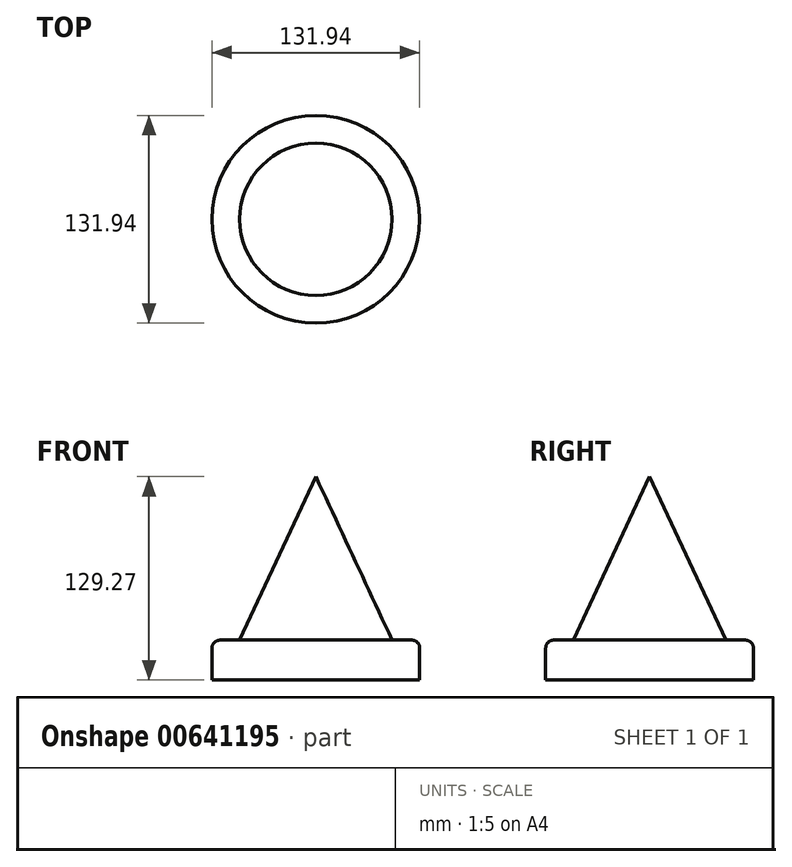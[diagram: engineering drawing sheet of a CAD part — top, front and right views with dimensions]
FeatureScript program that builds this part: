
annotation { "Feature Type Name" : "Feature", "Feature Type Description" : "" }
export const myFeature = defineFeature(function(context is Context, id is Id, definition is map)
    precondition{}
    {
        {
            var Q0;
            Q0=qCreatedBy(makeId("Top.planeOp"),FACE);
            var sketch = newSketch(context, id + "F0", { "sketchPlane" : qUnion([Q0])});
            skCircle(sketch, "E0", {"center": v(0, 0) * mm, "radius": 65.97 * mm});
            skSolve(sketch);
        }
        {
            var Q0;
            Q0=makeQuery(id+"F0.imprint","IMPRINT",FACE,{"disambiguationData":[TD([[makeQuery(id+"F0.imprint","IMPRINT",EDGE,{"derivedFrom":sQuery(id+"F0.wireOp",EDGE,"E0")}),1.0]])]});
            extrude(context, id + "F1", {"entities" : qUnion([Q0]), "depth" : 25.4 * mm, "offsetDistance" : 25.4 * mm});
        }
        {
            var Q0;
            Q0=qCreatedBy(makeId("Top.planeOp"),FACE);
            var sketch = newSketch(context, id + "F2", { "sketchPlane" : qUnion([Q0])});
            skCircle(sketch, "E1", {"center": v(0, 0) * mm, "radius": 57.16 * mm});
            skSolve(sketch);
        }
        {
            var Q0;
            Q0 = qSketchRegion(id + "F2", true);
            extrude(context, id + "F3", {"entities" : qUnion([Q0]), "operationType" : NewBodyOperationType.REMOVE, "oppositeDirection" : true, "depth" : 17.78 * mm, "offsetDistance" : 25.4 * mm});
        }
        {
            var Q0;
            Q0=makeQuery(id+"F1.opExtrude","CAP_FACE",FACE,{"disambiguationData":[OSD([sQuery(id+"F0.wireOp",EDGE,"E0")])],"isStart":false});
            var sketch = newSketch(context, id + "F4", { "sketchPlane" : qUnion([Q0])});
            skCircle(sketch, "E2", {"center": v(0, 0) * mm, "radius": 55.56 * mm});
            skSolve(sketch);
        }
        {
            var Q0;
            Q0=makeQuery(id+"F4.imprint","IMPRINT",FACE,{"disambiguationData":[TD([[makeQuery(id+"F4.imprint","IMPRINT",EDGE,{"derivedFrom":sQuery(id+"F4.wireOp",EDGE,"E2")}),1.0]])]});
            var sketch = newSketch(context, id + "F5", { "sketchPlane" : qUnion([Q0])});
            skSolve(sketch);
        }
        {
            var Q0;
            Q0=makeQuery(id+"F4.imprint","IMPRINT",FACE,{"disambiguationData":[TD([[makeQuery(id+"F4.imprint","IMPRINT",EDGE,{"derivedFrom":sQuery(id+"F4.wireOp",EDGE,"E2")}),1.0]])]});
            var Q1;
            Q1=makeQuery(id+"F4.imprint","IMPRINT",FACE,{"disambiguationData":[TD([[makeQuery(id+"F4.imprint","IMPRINT",EDGE,{"derivedFrom":sQuery(id+"F4.wireOp",EDGE,"E2")}),-1.0]])]});
            extrude(context, id + "F6", {"entities" : qUnion([Q0, Q1]), "operationType" : NewBodyOperationType.REMOVE, "depth" : 65.85 * mm, "offsetDistance" : 25.4 * mm});
        }
        {
            var Q0;
            Q0=makeQuery(id+"F1.opExtrude","CAP_EDGE",EDGE,{"disambiguationData":[OSD([sQuery(id+"F0.wireOp",EDGE,"E0")])],"isStart":false});
            fillet(context, id + "F7", {"entities" : qUnion([Q0]), "radius" : 5.08 * mm, "tangentPropagation" : true, "allowEdgeOverflow" : false});
        }
        {
            var Q0;
            Q0=qCreatedBy(makeId("Top.planeOp"),FACE);
            var sketch = newSketch(context, id + "F8", { "sketchPlane" : qUnion([Q0])});
            skCircle(sketch, "E3", {"center": v(0, 0) * mm, "radius": 62.08 * mm});
            skSolve(sketch);
        }
        {
            var Q0;
            Q0=makeQuery(id+"F8.imprint","IMPRINT",FACE,{"disambiguationData":[TD([[makeQuery(id+"F8.imprint","IMPRINT",EDGE,{"derivedFrom":sQuery(id+"F8.wireOp",EDGE,"E3")}),1.0]])]});
            var sketch = newSketch(context, id + "F9", { "sketchPlane" : qUnion([Q0])});
            skCircle(sketch, "E4", {"center": v(0, 0) * mm, "radius": 61.03 * mm});
            skSolve(sketch);
        }
        {
            var Q0;
            Q0=makeQuery(id+"F9.imprint","IMPRINT",FACE,{"disambiguationData":[TD([[makeQuery(id+"F9.imprint","IMPRINT",EDGE,{"derivedFrom":sQuery(id+"F9.wireOp",EDGE,"E4")}),1.0]])]});
            var sketch = newSketch(context, id + "F10", { "sketchPlane" : qUnion([Q0])});
            skCircle(sketch, "E5", {"center": v(0, 0) * mm, "radius": 60.28 * mm});
            skSolve(sketch);
        }
        {
            var Q0;
            Q0 = qSketchRegion(id + "F10", true);
            extrude(context, id + "F11", {"entities" : qUnion([Q0]), "operationType" : NewBodyOperationType.ADD, "depth" : 203.2 * mm, "offsetDistance" : 25.4 * mm, "hasDraft" : true, "draftAngle" : 25 * degree, "draftPullDirection" : true});
        }
    });
